# Revit family: QMXD_Horizontal
name_source: partatom
category: Mechanical Equipment
units: mm (PartAtom-declared; Revit-internal decimal feet)

## family parameters
Always vertical = Yes
Cut with Voids When Loaded = No
Part Type = Normal
Room Calculation Point = No
Round Connector Dimension = Use Radius
Shared = No
Work Plane-Based = No

## types (18) — shared parameters
0 = 0' - 0"
1.5 = 0' - 1 1/2"
1.9375 = 0' - 1 15/16"
3 = 0' - 3"
45 = 45.00°
Manufacturer = Loren Cook Company
Model = QMXD
ONE EIGTH = 0' - 0 1/8"
Type Comments = Mixed Flow Inline Horizontal Mount Direct Drive
URL = www.lorencook.com

## per-type parameters (varying)
| type | (A/2)-.125 | (F+3)/2 | (G/2)-.75 | -(B/2) | -(G/2)-.75 | A | A/2 | B | B/2 | B/6 | C | C/2 | D | E | F | F/2 | G | G/2 | H | H/2 |
| 90-QMXD_HOR | 0' - 6 9/32" | 0' - 7 11/16" | 0' - 8 7/16" | -0' - 9 15/16" | -0' - 8 7/16" | 1' - 0 13/16" | 0' - 6 13/32" | 1' - 7 7/8" | 0' - 9 15/16" | 0' - 3 5/16" | 1' - 3 7/8" | 0' - 7 15/16" | 0' - 8 1/2" | 2' - 7 1/4" | 1' - 0 3/8" | 0' - 6 3/16" | 1' - 6 3/8" | 0' - 9 3/16" | 0' - 0 1/2" | 0' - 0 1/4" |
| 120-QMXD_HOR | 0' - 8 13/32" | 0' - 9 1/4" | 0' - 10 1/2" | -1' - 0" | -0' - 10 1/2" | 1' - 5 1/16" | 0' - 8 17/32" | 2' - 0" | 1' - 0" | 0' - 4" | 1' - 8 1/16" | 0' - 10 1/32" | 0' - 10 1/2" | 3' - 0 11/16" | 1' - 3 1/2" | 0' - 7 3/4" | 1' - 10 1/2" | 0' - 11 1/4" | 0' - 0 1/2" | 0' - 0 1/4" |
| 135-QMXD_HOR | 0' - 9 1/2" | 0' - 10 1/4" | 1' - 0" | -1' - 1 1/2" | -1' - 0" | 1' - 7 1/4" | 0' - 9 5/8" | 2' - 3" | 1' - 1 1/2" | 0' - 4 1/2" | 1' - 10 1/4" | 0' - 11 1/8" | 1' - 0" | 3' - 3 1/2" | 1' - 5 1/2" | 0' - 8 3/4" | 2' - 1 1/2" | 1' - 0 3/4" | 0' - 0 1/2" | 0' - 0 1/4" |
| 150-QMXD_HOR | 0' - 10 9/16" | 0' - 10 7/8" | 1' - 1 9/16" | -1' - 3" | -1' - 1 9/16" | 1' - 9 3/8" | 0' - 10 11/16" | 2' - 6" | 1' - 3" | 0' - 5" | 2' - 0 3/8" | 1' - 0 3/16" | 1' - 1 3/16" | 3' - 6 1/16" | 1' - 6 3/4" | 0' - 9 3/8" | 2' - 4 5/8" | 1' - 2 5/16" | 0' - 0 1/2" | 0' - 0 1/4" |
| 165-QMXD_HOR | 0' - 11 5/8" | 0' - 11 29/32" | 1' - 3 1/16" | -1' - 4 1/2" | -1' - 3 1/16" | 1' - 11 1/2" | 0' - 11 3/4" | 2' - 9" | 1' - 4 1/2" | 0' - 5 1/2" | 2' - 2 1/2" | 1' - 1 1/4" | 1' - 2 5/16" | 3' - 7 3/4" | 1' - 8 13/16" | 0' - 10 13/32" | 2' - 7 5/8" | 1' - 3 13/16" | 0' - 0 1/2" | 0' - 0 1/4" |
| 180-QMXD_HOR | 1' - 0 11/16" | 1' - 0 29/32" | 1' - 4 1/16" | -1' - 5 1/2" | -1' - 4 1/16" | 2' - 1 5/8" | 1' - 0 13/16" | 2' - 11" | 1' - 5 1/2" | 0' - 5 27/32" | 2' - 4 5/8" | 1' - 2 5/16" | 1' - 3 1/2" | 3' - 10 1/4" | 1' - 10 13/16" | 0' - 11 13/32" | 2' - 9 5/8" | 1' - 4 13/16" | 0' - 0 9/16" | 0' - 0 9/32" |
| 202-QMXD_HOR | 1' - 2 1/4" | 1' - 1 5/8" | 1' - 5 5/16" | -1' - 6 3/4" | -1' - 5 5/16" | 2' - 4 3/4" | 1' - 2 3/8" | 3' - 1 1/2" | 1' - 6 3/4" | 0' - 6 1/4" | 2' - 7 3/4" | 1' - 3 7/8" | 1' - 5 1/4" | 4' - 1 15/16" | 2' - 0 1/4" | 1' - 0 1/8" | 3' - 0 1/8" | 1' - 6 1/16" | 0' - 0 9/16" | 0' - 0 9/32" |
| 225-QMXD_HOR | 1' - 3 27/32" | 1' - 2 31/32" | 1' - 7 1/16" | -1' - 8 1/2" | -1' - 7 1/16" | 2' - 7 15/16" | 1' - 3 31/32" | 3' - 5" | 1' - 8 1/2" | 0' - 6 27/32" | 2' - 10 15/16" | 1' - 5 15/32" | 1' - 7" | 4' - 7 13/16" | 2' - 2 15/16" | 1' - 1 15/32" | 3' - 3 5/8" | 1' - 7 13/16" | 0' - 0 9/16" | 0' - 0 9/32" |
| 245-QMXD_HOR | 1' - 5 1/4" | 1' - 3 31/32" | 1' - 8 13/16" | -1' - 10 1/4" | -1' - 8 13/16" | 2' - 10 3/4" | 1' - 5 3/8" | 3' - 8 1/2" | 1' - 10 1/4" | 0' - 7 13/32" | 3' - 1 3/4" | 1' - 6 7/8" | 1' - 8 1/2" | 4' - 11" | 2' - 4 15/16" | 1' - 2 15/32" | 3' - 7 1/8" | 1' - 9 9/16" | 0' - 0 11/16" | 0' - 0 11/32" |
| 270-QMXD_HOR | 1' - 7 1/32" | 1' - 5" | 1' - 10 1/16" | -1' - 11 1/2" | -1' - 10 1/16" | 3' - 2 5/16" | 1' - 7 5/32" | 3' - 11" | 1' - 11 1/2" | 0' - 7 27/32" | 3' - 5 5/16" | 1' - 8 21/32" | 1' - 10 7/16" | 5' - 2 7/8" | 2' - 7" | 1' - 3 1/2" | 3' - 9 5/8" | 1' - 10 13/16" | 0' - 0 11/16" | 0' - 0 11/32" |
| 300-QMXD_HOR | 1' - 9 1/8" | 1' - 6 3/8" | 2' - 1 9/16" | -2' - 3" | -2' - 1 9/16" | 3' - 6 1/2" | 1' - 9 1/4" | 4' - 6" | 2' - 3" | 0' - 9" | 3' - 9 1/2" | 1' - 10 3/4" | 2' - 0 3/4" | 5' - 8 1/16" | 2' - 9 3/4" | 1' - 4 7/8" | 4' - 4 5/8" | 2' - 2 5/16" | 0' - 0 11/16" | 0' - 0 11/32" |
| 330-QMXD_HOR | 1' - 11 1/4" | 1' - 7 7/8" | 2' - 3 13/16" | -2' - 5 1/4" | -2' - 3 13/16" | 3' - 10 3/4" | 1' - 11 3/8" | 4' - 10 1/2" | 2' - 5 1/4" | 0' - 9 3/4" | 4' - 1 3/4" | 2' - 0 7/8" | 2' - 3" | 6' - 2 13/16" | 3' - 0 3/4" | 1' - 6 3/8" | 4' - 9 1/8" | 2' - 4 9/16" | 0' - 0 11/16" | 0' - 0 11/32" |
| 365-QMXD_HOR | 2' - 1 3/4" | 1' - 9 3/4" | 2' - 6 15/16" | -2' - 8" | -2' - 6 15/16" | 4' - 3 3/4" | 2' - 1 7/8" | 5' - 4" | 2' - 8" | 0' - 10 21/32" | 4' - 6 3/4" | 2' - 3 3/8" | 2' - 5 13/16" | 6' - 8 1/4" | 3' - 4 1/2" | 1' - 8 1/4" | 5' - 3 3/8" | 2' - 7 11/16" | 0' - 0 13/16" | 0' - 0 13/32" |
| 402-QMXD_HOR | 2' - 4 11/32" | 1' - 11 1/2" | 2' - 9 3/16" | -2' - 10 1/4" | -2' - 9 3/16" | 4' - 8 15/16" | 2' - 4 15/32" | 5' - 8 1/2" | 2' - 10 1/4" | 0' - 11 13/32" | 4' - 11 15/16" | 2' - 5 31/32" | 2' - 8 11/16" | 7' - 4 5/16" | 3' - 8" | 1' - 10" | 5' - 7 7/8" | 2' - 9 15/16" | 0' - 0 13/16" | 0' - 0 13/32" |
| 445-QMXD_HOR | 2' - 7 13/32" | 2' - 1 5/8" | 2' - 11 15/16" | -3' - 1" | -2' - 11 15/16" | 5' - 3 1/16" | 2' - 7 17/32" | 6' - 2" | 3' - 1" | 1' - 0 11/32" | 5' - 6 1/16" | 2' - 9 1/32" | 3' - 0" | 7' - 10 7/8" | 4' - 0 1/4" | 2' - 0 1/8" | 6' - 1 3/8" | 3' - 0 11/16" | 0' - 0 13/16" | 0' - 0 13/32" |
| 490-QMXD_HOR | 2' - 10 9/16" | 2' - 3 7/8" | 3' - 3 3/16" | -3' - 4 1/4" | -3' - 3 3/16" | 5' - 9 3/8" | 2' - 10 11/16" | 6' - 8 1/2" | 3' - 4 1/4" | 1' - 1 13/32" | 6' - 0 3/8" | 3' - 0 3/16" | 3' - 3 7/16" | 8' - 7 3/8" | 4' - 4 3/4" | 2' - 2 3/8" | 6' - 7 7/8" | 3' - 3 15/16" | 0' - 0 13/16" | 0' - 0 13/32" |
| 540-QMXD_HOR | 3' - 2 3/32" | 2' - 6 1/2" | 3' - 6 7/16" | -3' - 7 1/2" | -3' - 6 7/16" | 6' - 4 7/16" | 3' - 2 7/32" | 7' - 3" | 3' - 7 1/2" | 1' - 2 1/2" | 6' - 7 7/16" | 3' - 3 23/32" | 3' - 7 5/16" | 9' - 2 15/16" | 4' - 10" | 2' - 5" | 7' - 2 3/8" | 3' - 7 3/16" | 0' - 0 13/16" | 0' - 0 13/32" |
| 600-QMXD_HOR | 3' - 6 5/16" | 2' - 9 1/2" | 3' - 10 11/16" | -3' - 11 3/4" | -3' - 10 11/16" | 7' - 0 7/8" | 3' - 6 7/16" | 7' - 11 1/2" | 3' - 11 3/4" | 1' - 3 29/32" | 7' - 3 7/8" | 3' - 7 15/16" | 4' - 2" | 10' - 2 1/16" | 5' - 4" | 2' - 8" | 7' - 10 7/8" | 3' - 11 7/16" | 0' - 0 13/16" | 0' - 0 13/32" |
